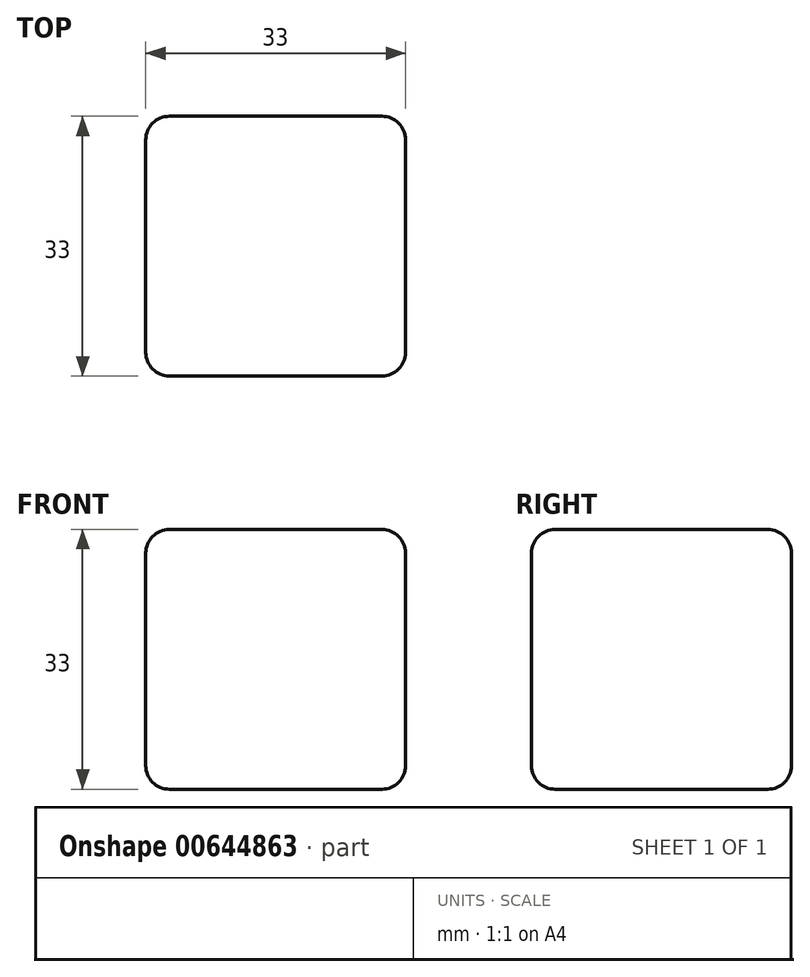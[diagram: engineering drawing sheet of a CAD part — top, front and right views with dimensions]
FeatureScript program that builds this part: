
annotation { "Feature Type Name" : "Feature", "Feature Type Description" : "" }
export const myFeature = defineFeature(function(context is Context, id is Id, definition is map)
    precondition{}
    {
        {
            var Q0;
            Q0=qCreatedBy(makeId("Top.planeOp"),FACE);
            var sketch = newSketch(context, id + "F0", { "sketchPlane" : qUnion([Q0])});
            skLineSegment(sketch, "E0.bottom", {"start": v(16.5, -16.5) * mm, "end": v(-16.5, -16.5) * mm});
            skLineSegment(sketch, "E0.top", {"start": v(16.5, 16.5) * mm, "end": v(-16.5, 16.5) * mm});
            skLineSegment(sketch, "E0.left", {"start": v(16.5, -16.5) * mm, "end": v(16.5, 16.5) * mm});
            skLineSegment(sketch, "E0.right", {"start": v(-16.5, -16.5) * mm, "end": v(-16.5, 16.5) * mm});
            skPoint(sketch, "E0.middle", {"position": v(0, 0) * mm});
            skSolve(sketch);
        }
        {
            var Q0;
            Q0 = qSketchRegion(id + "F0", true);
            extrude(context, id + "F1", {"entities" : qUnion([Q0]), "depth" : 33 * mm, "offsetDistance" : 25 * mm});
        }
        {
            var Q0;
            Q0=makeQuery(id+"F1.opExtrude","CAP_EDGE",EDGE,{"disambiguationData":[OSD([sQuery(id+"F0.wireOp",EDGE,"E0.right")])],"isStart":false});
            var Q1;
            Q1=makeQuery(id+"F1.opExtrude","CAP_EDGE",EDGE,{"disambiguationData":[OSD([sQuery(id+"F0.wireOp",EDGE,"E0.top")])],"isStart":false});
            var Q2;
            Q2=makeQuery(id+"F1.opExtrude","CAP_EDGE",EDGE,{"disambiguationData":[OSD([sQuery(id+"F0.wireOp",EDGE,"E0.left")])],"isStart":false});
            var Q3;
            Q3=makeQuery(id+"F1.opExtrude","CAP_EDGE",EDGE,{"disambiguationData":[OSD([sQuery(id+"F0.wireOp",EDGE,"E0.bottom")])],"isStart":false});
            var Q4;
            Q4=makeQuery(id+"F1.opExtrude","SWEPT_EDGE",EDGE,{"disambiguationData":[OSD([sQuery(id+"F0.wireOp",EDGE,"E0.bottom"),sQuery(id+"F0.wireOp",EDGE,"E0.left")])]});
            var Q5;
            Q5=makeQuery(id+"F1.opExtrude","CAP_EDGE",EDGE,{"disambiguationData":[OSD([sQuery(id+"F0.wireOp",EDGE,"E0.bottom")])],"isStart":true});
            var Q6;
            Q6=makeQuery(id+"F1.opExtrude","SWEPT_EDGE",EDGE,{"disambiguationData":[OSD([sQuery(id+"F0.wireOp",EDGE,"E0.bottom"),sQuery(id+"F0.wireOp",EDGE,"E0.right")])]});
            var Q7;
            Q7=makeQuery(id+"F1.opExtrude","CAP_EDGE",EDGE,{"disambiguationData":[OSD([sQuery(id+"F0.wireOp",EDGE,"E0.right")])],"isStart":true});
            var Q8;
            Q8=makeQuery(id+"F1.opExtrude","SWEPT_EDGE",EDGE,{"disambiguationData":[OSD([sQuery(id+"F0.wireOp",EDGE,"E0.top"),sQuery(id+"F0.wireOp",EDGE,"E0.right")])]});
            var Q9;
            Q9=makeQuery(id+"F1.opExtrude","CAP_EDGE",EDGE,{"disambiguationData":[OSD([sQuery(id+"F0.wireOp",EDGE,"E0.left")])],"isStart":true});
            var Q10;
            Q10=makeQuery(id+"F1.opExtrude","SWEPT_EDGE",EDGE,{"disambiguationData":[OSD([sQuery(id+"F0.wireOp",EDGE,"E0.top"),sQuery(id+"F0.wireOp",EDGE,"E0.left")])]});
            var Q11;
            Q11=makeQuery(id+"F1.opExtrude","CAP_EDGE",EDGE,{"disambiguationData":[OSD([sQuery(id+"F0.wireOp",EDGE,"E0.top")])],"isStart":true});
            fillet(context, id + "F2", {"entities" : qUnion([Q0, Q1, Q2, Q3, Q4, Q5, Q6, Q7, Q8, Q9, Q10, Q11]), "radius" : 3 * mm, "tangentPropagation" : true, "allowEdgeOverflow" : false});
        }
    });
